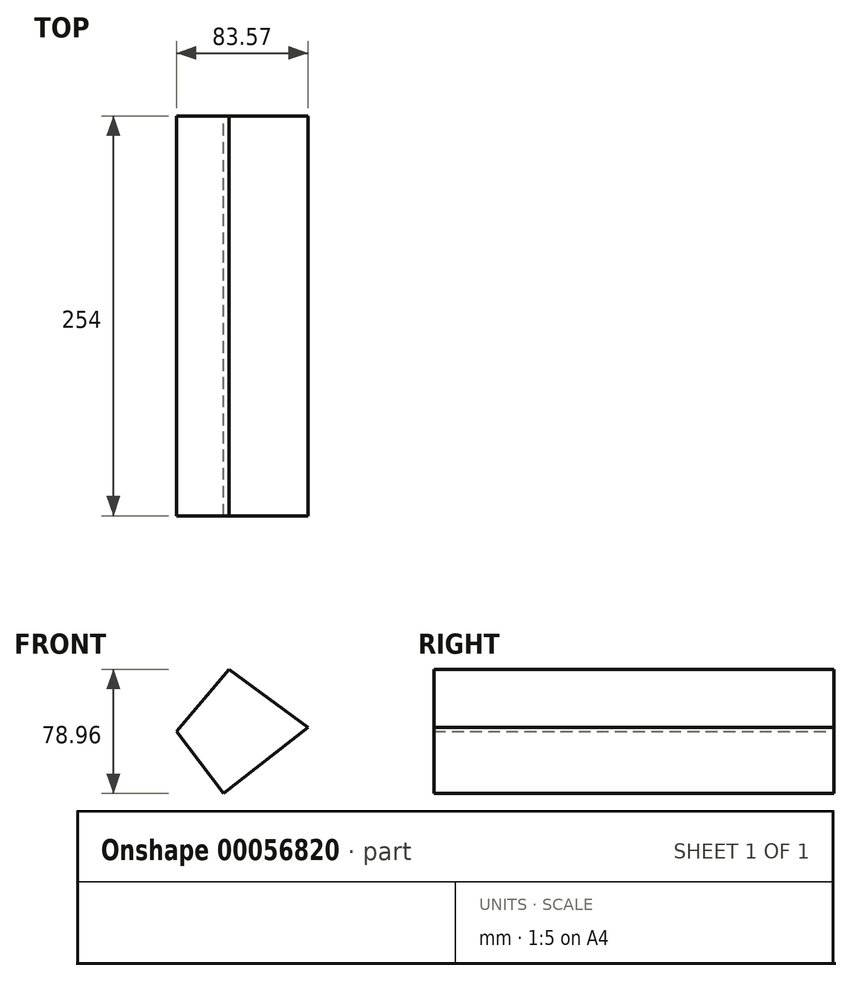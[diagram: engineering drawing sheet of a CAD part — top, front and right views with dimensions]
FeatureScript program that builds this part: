
annotation { "Feature Type Name" : "Feature", "Feature Type Description" : "" }
export const myFeature = defineFeature(function(context is Context, id is Id, definition is map)
    precondition{}
    {
        {
            var Q0;
            Q0=qCreatedBy(makeId("Front.planeOp"),FACE);
            var sketch = newSketch(context, id + "F0", { "sketchPlane" : qUnion([Q0])});
            skLineSegment(sketch, "E0", {"start": v(-117.68, -8.34) * mm, "end": v(-84.17, 31.21) * mm});
            skLineSegment(sketch, "E1", {"start": v(-84.17, 31.21) * mm, "end": v(-34.11, -5.6) * mm});
            skLineSegment(sketch, "E2", {"start": v(-34.11, -5.6) * mm, "end": v(-87.8, -47.75) * mm});
            skLineSegment(sketch, "E3", {"start": v(-87.8, -47.75) * mm, "end": v(-117.68, -8.34) * mm});
            skSolve(sketch);
        }
        {
            var Q0;
            Q0=makeQuery(id+"F0.imprint","IMPRINT",FACE,{"disambiguationData":[TD([[makeQuery(id+"F0.imprint","IMPRINT",EDGE,{"derivedFrom":sQuery(id+"F0.wireOp",EDGE,"E0")}),-1.0]])]});
            extrude(context, id + "F1", {"entities" : qUnion([Q0]), "depth" : 254 * mm});
        }
    });
